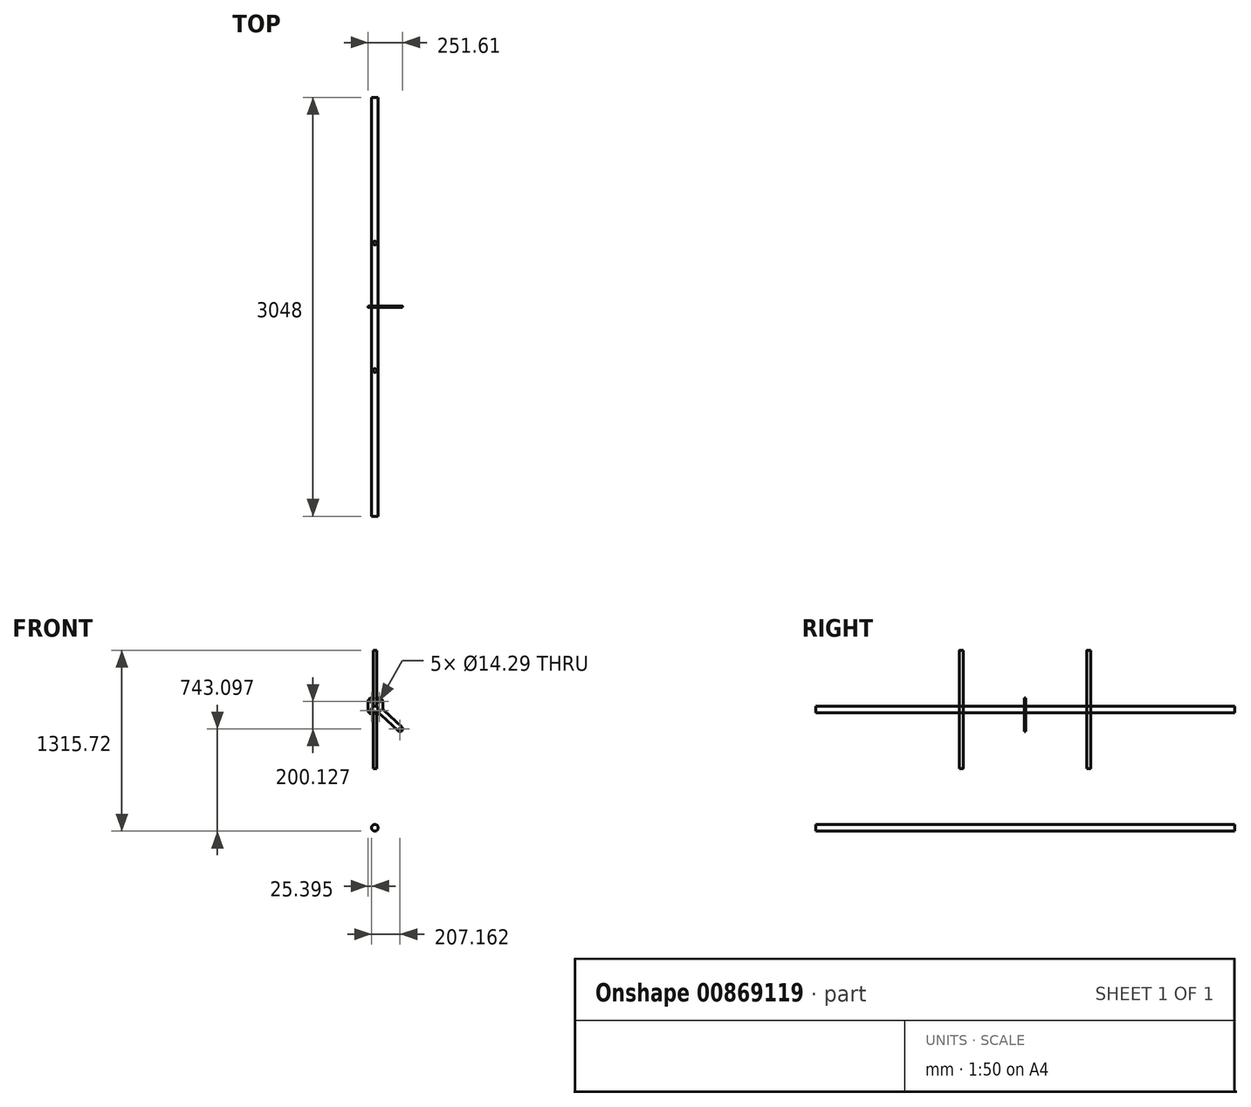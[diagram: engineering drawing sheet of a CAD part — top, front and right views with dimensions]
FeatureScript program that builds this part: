
annotation { "Feature Type Name" : "Feature", "Feature Type Description" : "" }
export const myFeature = defineFeature(function(context is Context, id is Id, definition is map)
    precondition{}
    {
        {
            var Q0;
            Q0=qCreatedBy(makeId("Front.planeOp"),FACE);
            var sketch = newSketch(context, id + "F0", { "sketchPlane" : qUnion([Q0])});
            skLineSegment(sketch, "E0.bottom", {"start": v(-23.73, 83.43) * mm, "end": v(31.51, 83.43) * mm});
            skLineSegment(sketch, "E0.top", {"start": v(-23.73, -33.1) * mm, "end": v(28.49, -33.1) * mm});
            skLineSegment(sketch, "E0.left", {"start": v(-49.13, 58.03) * mm, "end": v(-49.13, -7.7) * mm});
            skLineSegment(sketch, "E0.right", {"start": v(56.91, 58.03) * mm, "end": v(56.91, 12.69) * mm});
            skCircle(sketch, "E1", {"center": v(183.43, -142.1) * mm, "radius": 7.14 * mm});
            skPoint(sketch, "E2.visualSharp", {"position": v(-49.13, 83.43) * mm});
            skArc(sketch, "E2.filletArc", {"start": v(-23.73, 83.43) * mm, "mid": v(-41.7, 76) * mm, "end": v(-49.13, 58.03) * mm});
            skPoint(sketch, "E3.visualSharp", {"position": v(56.91, 83.43) * mm});
            skArc(sketch, "E3.filletArc", {"start": v(56.91, 58.03) * mm, "mid": v(49.47, 76) * mm, "end": v(31.51, 83.43) * mm});
            skPoint(sketch, "E4.visualSharp", {"position": v(-49.13, -33.1) * mm});
            skArc(sketch, "E4.filletArc", {"start": v(-49.13, -7.7) * mm, "mid": v(-41.7, -25.66) * mm, "end": v(-23.73, -33.1) * mm});
            skLineSegment(sketch, "E5", {"start": v(-49.13, -33.1) * mm, "end": v(56.91, 83.43) * mm, "construction": true});
            skLineSegment(sketch, "E6", {"start": v(3.89, 25.17) * mm, "end": v(183.43, -142.1) * mm, "construction": true});
            skArc(sketch, "E7", {"start": v(170.44, -156.03) * mm, "mid": v(198.09, -154.26) * mm, "end": v(194.74, -126.76) * mm});
            skLineSegment(sketch, "E8", {"start": v(194.74, -126.76) * mm, "end": v(65, -5.9) * mm});
            skLineSegment(sketch, "E9", {"start": v(170.44, -156.03) * mm, "end": v(45.8, -39.92) * mm});
            skArc(sketch, "E10.filletArc", {"start": v(56.91, 12.69) * mm, "mid": v(59.02, 2.55) * mm, "end": v(65, -5.9) * mm});
            skArc(sketch, "E11.filletArc", {"start": v(45.8, -39.92) * mm, "mid": v(37.8, -34.87) * mm, "end": v(28.49, -33.1) * mm});
            skCircle(sketch, "E12", {"center": v(-23.73, 58.03) * mm, "radius": 7.14 * mm});
            skCircle(sketch, "E13.0.1.0", {"center": v(-23.73, -7.7) * mm, "radius": 7.14 * mm});
            skCircle(sketch, "E13.1.0.0", {"center": v(31.51, 58.03) * mm, "radius": 7.14 * mm});
            skCircle(sketch, "E13.1.1.0", {"center": v(31.51, -7.7) * mm, "radius": 7.14 * mm});
            skLineSegment(sketch, "E13.direction1", {"start": v(-23.73, 58.03) * mm, "end": v(31.51, 58.03) * mm, "construction": true});
            skLineSegment(sketch, "E13.direction2", {"start": v(-23.73, 58.03) * mm, "end": v(-23.73, -7.7) * mm, "construction": true});
            skSolve(sketch);
        }
        {
            var Q0;
            Q0=makeQuery(id+"F0.imprint","IMPRINT",FACE,{"disambiguationData":[TD([[makeQuery(id+"F0.imprint","IMPRINT",EDGE,{"derivedFrom":sQuery(id+"F0.wireOp",EDGE,"E0.bottom")}),-1.0]])]});
            extrude(context, id + "F1", {"entities" : qUnion([Q0]), "endBound" : BoundingType.SYMMETRIC, "depth" : 9.52 * mm, "offsetDistance" : 25.4 * mm});
        }
        {
            var Q0;
            Q0=qCreatedBy(makeId("Front.planeOp"),FACE);
            var sketch = newSketch(context, id + "F2", { "sketchPlane" : qUnion([Q0])});
            skCircle(sketch, "E14", {"center": v(0, 0) * mm, "radius": 24.13 * mm});
            skCircle(sketch, "E15", {"center": v(0, -861.06) * mm, "radius": 24.13 * mm});
            skSolve(sketch);
        }
        {
            var Q0;
            Q0 = qSketchRegion(id + "F2", true);
            extrude(context, id + "F3", {"entities" : qUnion([Q0]), "endBound" : BoundingType.SYMMETRIC, "depth" : 3048 * mm, "offsetDistance" : 25.4 * mm});
        }
        {
            var Q0;
            Q0=qCreatedBy(makeId("Top.planeOp"),FACE);
            var sketch = newSketch(context, id + "F4", { "sketchPlane" : qUnion([Q0])});
            skCircle(sketch, "E16", {"center": v(0, 463.55) * mm, "radius": 13.34 * mm});
            skLineSegment(sketch, "E17", {"start": v(-316.47, 0) * mm, "end": v(287.14, 0) * mm, "construction": true});
            skCircle(sketch, "E18.MirrorC", {"center": v(0, -463.55) * mm, "radius": 13.34 * mm});
            skSolve(sketch);
        }
        {
            var Q0;
            Q0 = qSketchRegion(id + "F4", true);
            extrude(context, id + "F5", {"entities" : qUnion([Q0]), "endBound" : BoundingType.SYMMETRIC, "depth" : 861.06 * mm, "offsetDistance" : 25.4 * mm});
        }
    });
